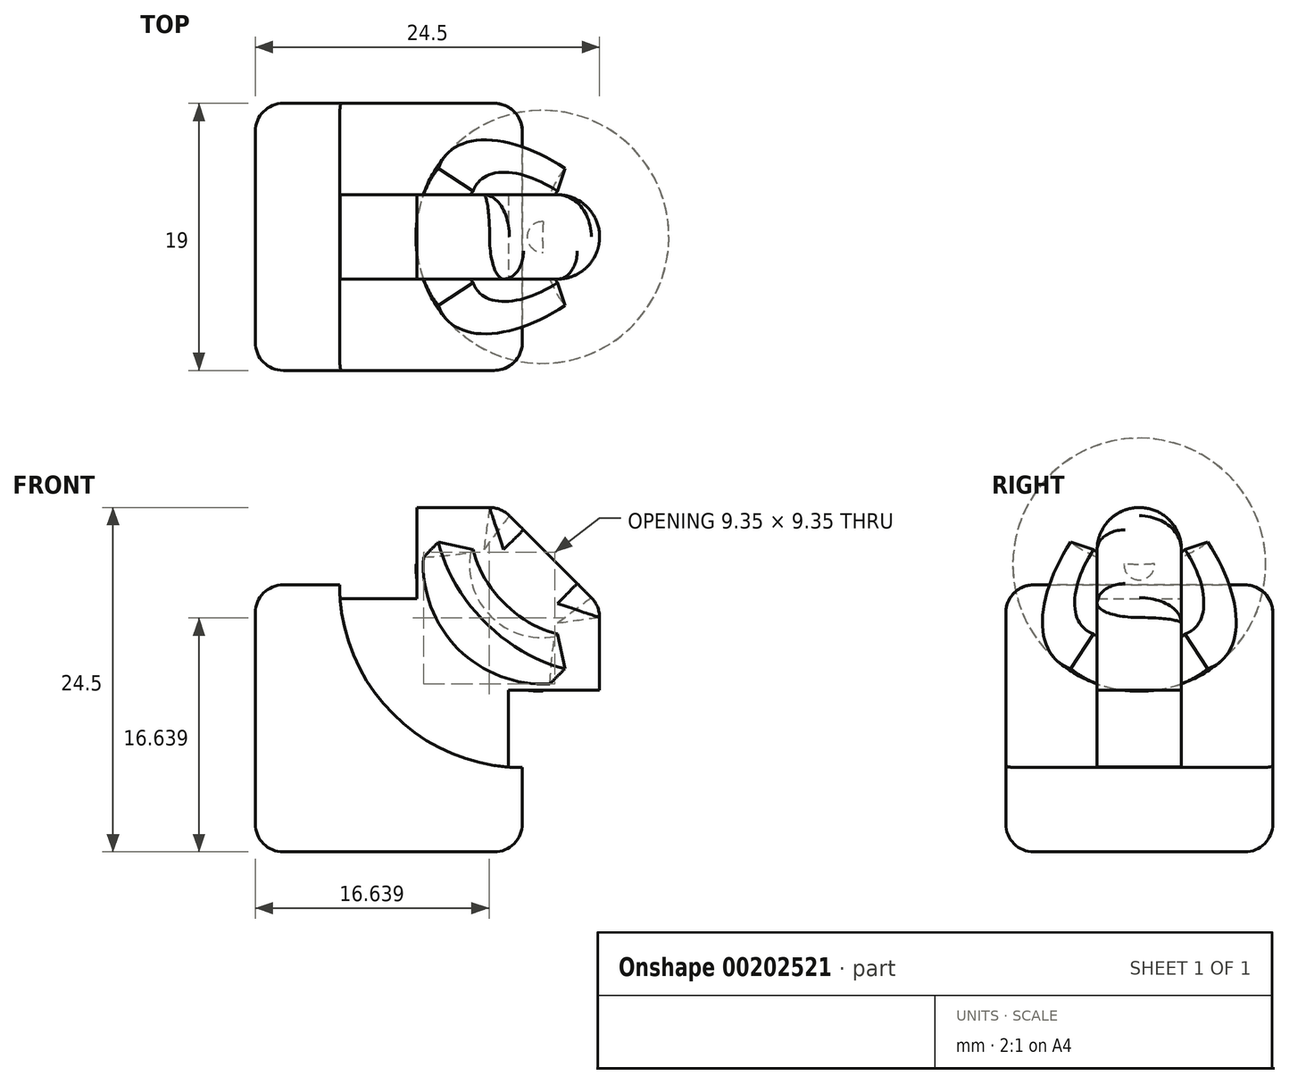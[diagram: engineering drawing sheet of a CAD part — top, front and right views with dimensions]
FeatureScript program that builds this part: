
annotation { "Feature Type Name" : "Feature", "Feature Type Description" : "" }
export const myFeature = defineFeature(function(context is Context, id is Id, definition is map)
    precondition{}
    {
        {
            var Q0;
            Q0=qCreatedBy(makeId("Front.planeOp"),FACE);
            var sketch = newSketch(context, id + "F0", { "sketchPlane" : qUnion([Q0])});
            skLineSegment(sketch, "E0.bottom", {"start": v(0, 0) * mm, "end": v(19, 0) * mm});
            skLineSegment(sketch, "E0.top", {"start": v(0, 19) * mm, "end": v(19, 19) * mm});
            skLineSegment(sketch, "E0.left", {"start": v(0, 0) * mm, "end": v(0, 19) * mm});
            skLineSegment(sketch, "E0.right", {"start": v(19, 0) * mm, "end": v(19, 19) * mm});
            skSolve(sketch);
        }
        {
            var Q0;
            Q0 = qSketchRegion(id + "F0", true);
            extrude(context, id + "F1", {"entities" : qUnion([Q0]), "depth" : 19 * mm, "symmetric" : true});
        }
        {
            var Q0;
            Q0=makeQuery(id+"F1.opExtrude","CAP_FACE",FACE,{"disambiguationData":[OSD([sQuery(id+"F0.wireOp",EDGE,"E0.bottom"),sQuery(id+"F0.wireOp",EDGE,"E0.top"),sQuery(id+"F0.wireOp",EDGE,"E0.left"),sQuery(id+"F0.wireOp",EDGE,"E0.right")])],"isStart":false});
            var sketch = newSketch(context, id + "F2", { "sketchPlane" : qUnion([Q0])});
            skArc(sketch, "E1", {"start": v(19, 6) * mm, "mid": v(9.8, 9.8) * mm, "end": v(6, 19) * mm});
            skLineSegment(sketch, "E2", {"start": v(19, 6) * mm, "end": v(19, 19) * mm});
            skLineSegment(sketch, "E3", {"start": v(6, 19) * mm, "end": v(19, 19) * mm});
            skSolve(sketch);
        }
        {
            var Q0;
            Q0 = qSketchRegion(id + "F2", true);
            extrude(context, id + "F3", {"entities" : qUnion([Q0]), "operationType" : NewBodyOperationType.REMOVE, "endBound" : BoundingType.THROUGH_ALL, "oppositeDirection" : true, "depth" : 25 * mm});
        }
        {
            var Q0;
            Q0=qCreatedBy(makeId("Front.planeOp"),FACE);
            var sketch = newSketch(context, id + "F4", { "sketchPlane" : qUnion([Q0])});
            skLineSegment(sketch, "E4", {"start": v(0, 0) * mm, "end": v(0, 18) * mm});
            skLineSegment(sketch, "E5", {"start": v(0, 18) * mm, "end": v(11.5, 18) * mm});
            skLineSegment(sketch, "E6", {"start": v(11.5, 18) * mm, "end": v(11.5, 24.5) * mm});
            skLineSegment(sketch, "E7", {"start": v(11.5, 24.5) * mm, "end": v(24.5, 24.5) * mm});
            skLineSegment(sketch, "E8", {"start": v(24.5, 24.5) * mm, "end": v(24.5, 11.5) * mm});
            skLineSegment(sketch, "E9", {"start": v(24.5, 11.5) * mm, "end": v(18, 11.5) * mm});
            skLineSegment(sketch, "E10", {"start": v(18, 11.5) * mm, "end": v(18, 0) * mm});
            skLineSegment(sketch, "E11", {"start": v(18, 0) * mm, "end": v(0, 0) * mm});
            skSolve(sketch);
        }
        {
            var Q0;
            Q0 = qSketchRegion(id + "F4", true);
            extrude(context, id + "F5", {"entities" : qUnion([Q0]), "operationType" : NewBodyOperationType.ADD, "depth" : 6 * mm, "symmetric" : true});
        }
        {
            var Q0;
            Q0=makeQuery(id+"F1.opExtrude","SWEPT_EDGE",EDGE,{"disambiguationData":[OSD([sQuery(id+"F0.wireOp",EDGE,"E0.bottom"),sQuery(id+"F0.wireOp",EDGE,"E0.left")])]});
            fillet(context, id + "F6", {"entities" : qUnion([Q0]), "radius" : 2 * mm, "tangentPropagation" : true, "allowEdgeOverflow" : false});
        }
        {
            var Q0;
            Q0=makeQuery(id+"F5.opExtrude","CAP_FACE",FACE,{"disambiguationData":[OSD([sQuery(id+"F4.wireOp",EDGE,"E4"),sQuery(id+"F4.wireOp",EDGE,"E5"),sQuery(id+"F4.wireOp",EDGE,"E6"),sQuery(id+"F4.wireOp",EDGE,"E7"),sQuery(id+"F4.wireOp",EDGE,"E8"),sQuery(id+"F4.wireOp",EDGE,"E9"),sQuery(id+"F4.wireOp",EDGE,"E10"),sQuery(id+"F4.wireOp",EDGE,"E11")])],"isStart":false});
            var sketch = newSketch(context, id + "F7", { "sketchPlane" : qUnion([Q0])});
            skLineSegment(sketch, "E12", {"start": v(24.5, 11.5) * mm, "end": v(24.5, 17.5) * mm});
            skLineSegment(sketch, "E13", {"start": v(24.5, 17.5) * mm, "end": v(17.5, 24.5) * mm});
            skLineSegment(sketch, "E14", {"start": v(17.5, 24.5) * mm, "end": v(11.5, 24.5) * mm});
            skLineSegment(sketch, "E15", {"start": v(11.5, 24.5) * mm, "end": v(11.5, 11.5) * mm});
            skLineSegment(sketch, "E16", {"start": v(11.5, 11.5) * mm, "end": v(24.5, 11.5) * mm});
            skLineSegment(sketch, "E17", {"start": v(24.5, 17.5) * mm, "end": v(24.5, 24.5) * mm});
            skLineSegment(sketch, "E18", {"start": v(24.5, 24.5) * mm, "end": v(17.5, 24.5) * mm});
            skSolve(sketch);
        }
        {
            var Q0;
            Q0=makeQuery(id+"F7.imprint","IMPRINT",FACE,{"disambiguationData":[TD([[makeQuery(id+"F7.imprint","IMPRINT",EDGE,{"derivedFrom":sQuery(id+"F7.wireOp",EDGE,"E13")}),-1.0]])]});
            extrude(context, id + "F8", {"entities" : qUnion([Q0]), "operationType" : NewBodyOperationType.REMOVE, "endBound" : BoundingType.THROUGH_ALL, "oppositeDirection" : true, "depth" : 25 * mm});
        }
        {
            var Q0;
            Q0=makeQuery(id+"F1.opExtrude","CAP_EDGE",EDGE,{"disambiguationData":[OSD([sQuery(id+"F0.wireOp",EDGE,"E0.left")])],"isStart":false});
            var Q1;
            Q1=makeQuery(id+"F1.opExtrude","CAP_EDGE",EDGE,{"disambiguationData":[OSD([sQuery(id+"F0.wireOp",EDGE,"E0.left")])],"isStart":true});
            var Q2;
            Q2=makeQuery(id+"F1.opExtrude","SWEPT_EDGE",EDGE,{"disambiguationData":[OSD([sQuery(id+"F0.wireOp",EDGE,"E0.top"),sQuery(id+"F0.wireOp",EDGE,"E0.left")])]});
            var Q3;
            Q3=makeQuery(id+"F1.opExtrude","CAP_EDGE",EDGE,{"disambiguationData":[OSD([sQuery(id+"F0.wireOp",EDGE,"E0.top")])],"isStart":true});
            var Q4;
            Q4=makeQuery(id+"F1.opExtrude","CAP_EDGE",EDGE,{"disambiguationData":[OSD([sQuery(id+"F0.wireOp",EDGE,"E0.top")])],"isStart":false});
            var Q5;
            Q5=makeQuery(id+"F1.opExtrude","CAP_EDGE",EDGE,{"disambiguationData":[OSD([sQuery(id+"F0.wireOp",EDGE,"E0.right")])],"isStart":true});
            var Q6;
            Q6=makeQuery(id+"F1.opExtrude","SWEPT_EDGE",EDGE,{"disambiguationData":[OSD([sQuery(id+"F0.wireOp",EDGE,"E0.bottom"),sQuery(id+"F0.wireOp",EDGE,"E0.right")])]});
            var Q7;
            Q7=makeQuery(id+"F1.opExtrude","CAP_EDGE",EDGE,{"disambiguationData":[OSD([sQuery(id+"F0.wireOp",EDGE,"E0.right")])],"isStart":false});
            fillet(context, id + "F9", {"entities" : qUnion([Q0, Q1, Q2, Q3, Q4, Q5, Q6, Q7]), "radius" : 2 * mm, "tangentPropagation" : true, "allowEdgeOverflow" : false});
        }
        {
            var Q0;
            Q0=makeQuery(id+"F5.opExtrude","CAP_EDGE",EDGE,{"disambiguationData":[OSD([sQuery(id+"F4.wireOp",EDGE,"E7")])],"isStart":false});
            var Q1;
            Q1=makeQuery(id+"F8.boolean.opBoolean","COPY",EDGE,{"derivedFrom":makeQuery(id+"F8.opExtrude","CAP_EDGE",EDGE,{"disambiguationData":[OSD([sQuery(id+"F7.wireOp",EDGE,"E13")])],"isStart":true})});
            var Q2;
            Q2=makeQuery(id+"F5.opExtrude","CAP_EDGE",EDGE,{"disambiguationData":[OSD([sQuery(id+"F4.wireOp",EDGE,"E8")])],"isStart":false});
            var Q3;
            Q3=makeQuery(id+"F5.opExtrude","CAP_EDGE",EDGE,{"disambiguationData":[OSD([sQuery(id+"F4.wireOp",EDGE,"E7")])],"isStart":true});
            var Q4;
            Q4=makeQuery(id+"F8.boolean.opBoolean","INTERSECT",EDGE,{"derivedFrom":[makeQuery(id+"F5.opExtrude","CAP_FACE",FACE,{"disambiguationData":[OSD([sQuery(id+"F4.wireOp",EDGE,"E4"),sQuery(id+"F4.wireOp",EDGE,"E5"),sQuery(id+"F4.wireOp",EDGE,"E6"),sQuery(id+"F4.wireOp",EDGE,"E7"),sQuery(id+"F4.wireOp",EDGE,"E8"),sQuery(id+"F4.wireOp",EDGE,"E9"),sQuery(id+"F4.wireOp",EDGE,"E10"),sQuery(id+"F4.wireOp",EDGE,"E11")])],"isStart":true}),makeQuery(id+"F8.opExtrude","SWEPT_FACE",FACE,{"disambiguationData":[OSD([sQuery(id+"F7.wireOp",EDGE,"E13")])]})]});
            var Q5;
            Q5=makeQuery(id+"F5.opExtrude","CAP_EDGE",EDGE,{"disambiguationData":[OSD([sQuery(id+"F4.wireOp",EDGE,"E8")])],"isStart":true});
            fillet(context, id + "F10", {"entities" : qUnion([Q0, Q1, Q2, Q3, Q4, Q5]), "radius" : 3 * mm, "tangentPropagation" : true, "allowEdgeOverflow" : false});
        }
        {
            var Q0;
            {var subQ0=sQuery(id+"F4.wireOp",EDGE,"E7");Q0=makeQuery(id+"F10.opFillet","BLEND_EDGE",EDGE,{"blendedFrom":[makeQuery(id+"F8.boolean.opBoolean","INTERSECT",EDGE,{"derivedFrom":[makeQuery(id+"F5.opExtrude","CAP_FACE",FACE,{"disambiguationData":[OSD([sQuery(id+"F4.wireOp",EDGE,"E4"),sQuery(id+"F4.wireOp",EDGE,"E5"),sQuery(id+"F4.wireOp",EDGE,"E6"),subQ0,sQuery(id+"F4.wireOp",EDGE,"E8"),sQuery(id+"F4.wireOp",EDGE,"E9"),sQuery(id+"F4.wireOp",EDGE,"E10"),sQuery(id+"F4.wireOp",EDGE,"E11")])],"isStart":true}),makeQuery(id+"F8.opExtrude","SWEPT_FACE",FACE,{"disambiguationData":[OSD([sQuery(id+"F7.wireOp",EDGE,"E13")])]})]}),makeQuery(id+"F5.opExtrude","CAP_EDGE",EDGE,{"disambiguationData":[OSD([subQ0])],"isStart":true})],"blendedInto":[]});}
            var Q1;
            {var subQ0=sQuery(id+"F4.wireOp",EDGE,"E8");Q1=makeQuery(id+"F10.opFillet","BLEND_EDGE",EDGE,{"blendedFrom":[makeQuery(id+"F8.boolean.opBoolean","INTERSECT",EDGE,{"derivedFrom":[makeQuery(id+"F5.opExtrude","CAP_FACE",FACE,{"disambiguationData":[OSD([sQuery(id+"F4.wireOp",EDGE,"E4"),sQuery(id+"F4.wireOp",EDGE,"E5"),sQuery(id+"F4.wireOp",EDGE,"E6"),sQuery(id+"F4.wireOp",EDGE,"E7"),subQ0,sQuery(id+"F4.wireOp",EDGE,"E9"),sQuery(id+"F4.wireOp",EDGE,"E10"),sQuery(id+"F4.wireOp",EDGE,"E11")])],"isStart":true}),makeQuery(id+"F8.opExtrude","SWEPT_FACE",FACE,{"disambiguationData":[OSD([sQuery(id+"F7.wireOp",EDGE,"E13")])]})]}),makeQuery(id+"F5.opExtrude","CAP_EDGE",EDGE,{"disambiguationData":[OSD([subQ0])],"isStart":true})],"blendedInto":[]});}
            fillet(context, id + "F11", {"entities" : qUnion([Q0, Q1]), "radius" : 2 * mm, "tangentPropagation" : true, "allowEdgeOverflow" : false});
        }
        {
            var Q0;
            Q0=qCreatedBy(makeId("Front.planeOp"),FACE);
            var sketch = newSketch(context, id + "F12", { "sketchPlane" : qUnion([Q0])});
            skLineSegment(sketch, "E19", {"start": v(11.43, 20.43) * mm, "end": v(14.43, 20.43) * mm, "construction": true});
            skPoint(sketch, "E20", {"position": v(11.43, 20.43) * mm});
            skLineSegment(sketch, "E21", {"start": v(20.43, 14.43) * mm, "end": v(20.43, 11.43) * mm, "construction": true});
            skPoint(sketch, "E22", {"position": v(20.43, 11.43) * mm});
            skArc(sketch, "E23", {"start": v(11.43, 20.43) * mm, "mid": v(14.07, 14.07) * mm, "end": v(20.43, 11.43) * mm});
            skLineSegment(sketch, "E24", {"start": v(11.43, 20.43) * mm, "end": v(14.43, 20.43) * mm});
            skLineSegment(sketch, "E25", {"start": v(20.43, 11.43) * mm, "end": v(20.43, 14.43) * mm});
            skArc(sketch, "E26", {"start": v(14.43, 20.43) * mm, "mid": v(16.2, 16.2) * mm, "end": v(20.43, 14.43) * mm});
            skLineSegment(sketch, "E27", {"start": v(20.43, 14.43) * mm, "end": v(20.43, 11.43) * mm});
            skLineSegment(sketch, "E28", {"start": v(14.43, 20.43) * mm, "end": v(20.43, 14.43) * mm, "construction": true});
            skLineSegment(sketch, "E29", {"start": v(14.78, 26.1) * mm, "end": v(26.1, 14.78) * mm, "construction": true});
            skSolve(sketch);
        }
        {
            var Q0;
            Q0 = qSketchRegion(id + "F12", true);
            var Q1;
            Q1=sQuery(id+"F12.wireOp",EDGE,"E29");
            revolve(context, id + "F13", {"operationType" : NewBodyOperationType.ADD, "entities" : qUnion([Q0]), "axis" : qUnion([Q1]), "revolveType" : RevolveType.SYMMETRIC, "angle" : 100 * degree});
        }
    });
